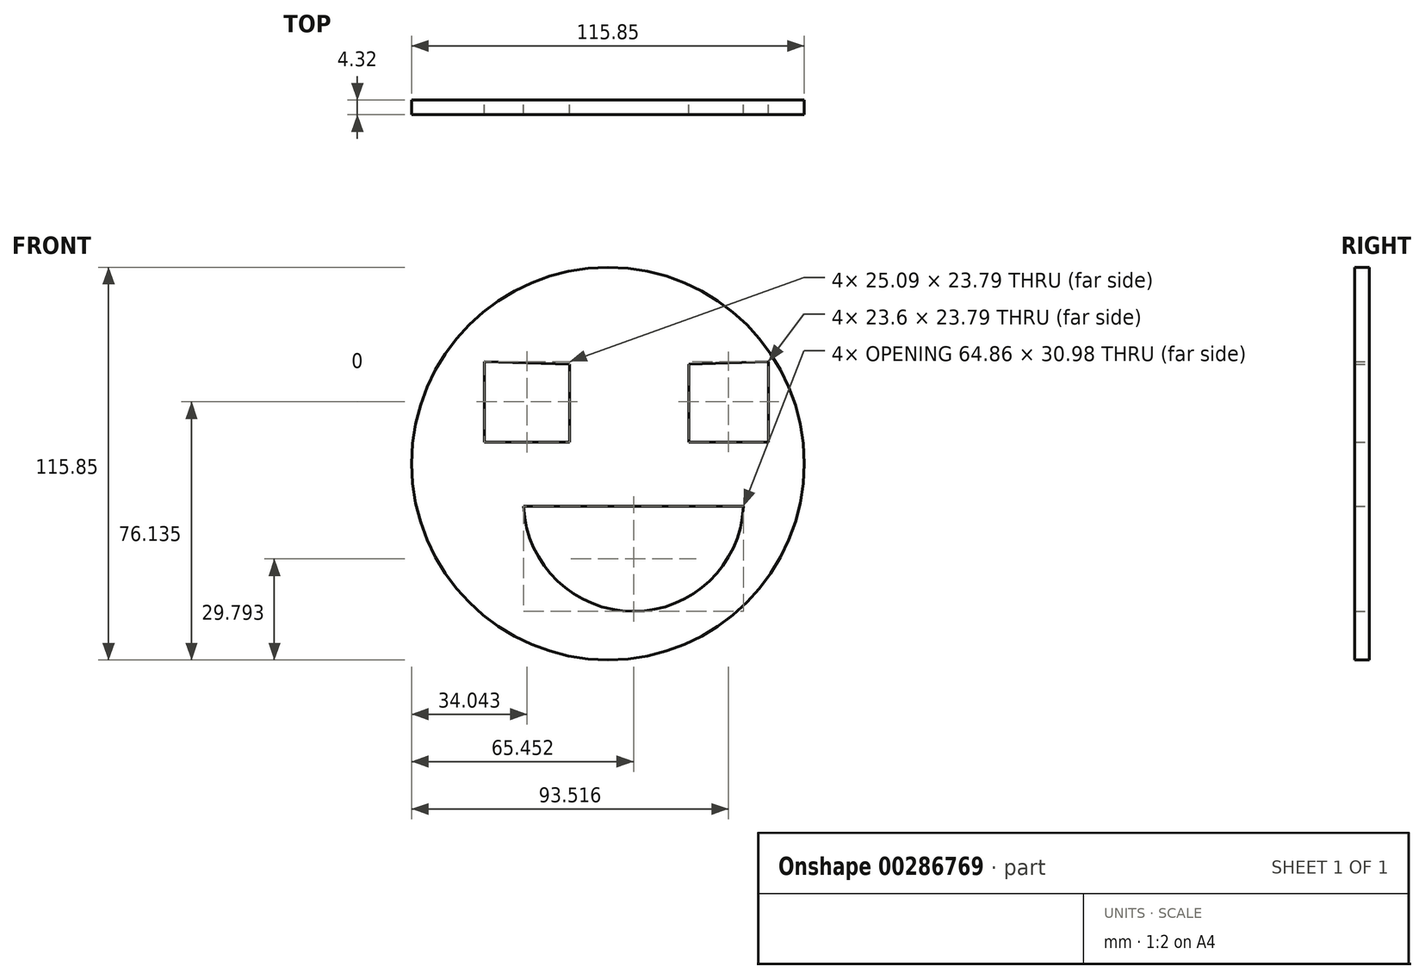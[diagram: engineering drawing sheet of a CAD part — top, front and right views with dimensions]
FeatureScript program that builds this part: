
annotation { "Feature Type Name" : "Feature", "Feature Type Description" : "" }
export const myFeature = defineFeature(function(context is Context, id is Id, definition is map)
    precondition{}
    {
        {
            var Q0;
            Q0=qCreatedBy(makeId("Front.planeOp"),FACE);
            var sketch = newSketch(context, id + "F0", { "sketchPlane" : qUnion([Q0])});
            skCircle(sketch, "E0", {"center": v(-8.74, 17.2) * mm, "radius": 57.92 * mm});
            skLineSegment(sketch, "E1", {"start": v(-45.16, 47.3) * mm, "end": v(-45.16, 23.51) * mm});
            skLineSegment(sketch, "E2", {"start": v(-45.16, 23.51) * mm, "end": v(-20.07, 23.51) * mm});
            skLineSegment(sketch, "E3", {"start": v(-20.07, 23.51) * mm, "end": v(-20.07, 46.56) * mm});
            skLineSegment(sketch, "E4", {"start": v(-20.07, 46.56) * mm, "end": v(-45.16, 47.3) * mm});
            skLineSegment(sketch, "E5", {"start": v(15.05, 46.56) * mm, "end": v(15.05, 23.51) * mm});
            skLineSegment(sketch, "E6", {"start": v(15.05, 23.51) * mm, "end": v(38.66, 23.51) * mm});
            skLineSegment(sketch, "E7", {"start": v(38.66, 23.51) * mm, "end": v(38.66, 47.3) * mm});
            skLineSegment(sketch, "E8", {"start": v(38.66, 47.3) * mm, "end": v(15.05, 46.56) * mm});
            skLineSegment(sketch, "E9", {"start": v(-33.64, 4.55) * mm, "end": v(31.22, 4.55) * mm});
            skArc(sketch, "E10", {"start": v(-33.64, 4.55) * mm, "mid": v(-1.2, -26.43) * mm, "end": v(31.22, 4.55) * mm});
            skSolve(sketch);
        }
        {
            var Q0;
            Q0=makeQuery(id+"F0.imprint","IMPRINT",FACE,{"disambiguationData":[TD([[makeQuery(id+"F0.imprint","IMPRINT",EDGE,{"derivedFrom":sQuery(id+"F0.wireOp",EDGE,"E0")}),1.0]])]});
            extrude(context, id + "F1", {"entities" : qUnion([Q0]), "depth" : 4.32 * mm});
        }
    });
